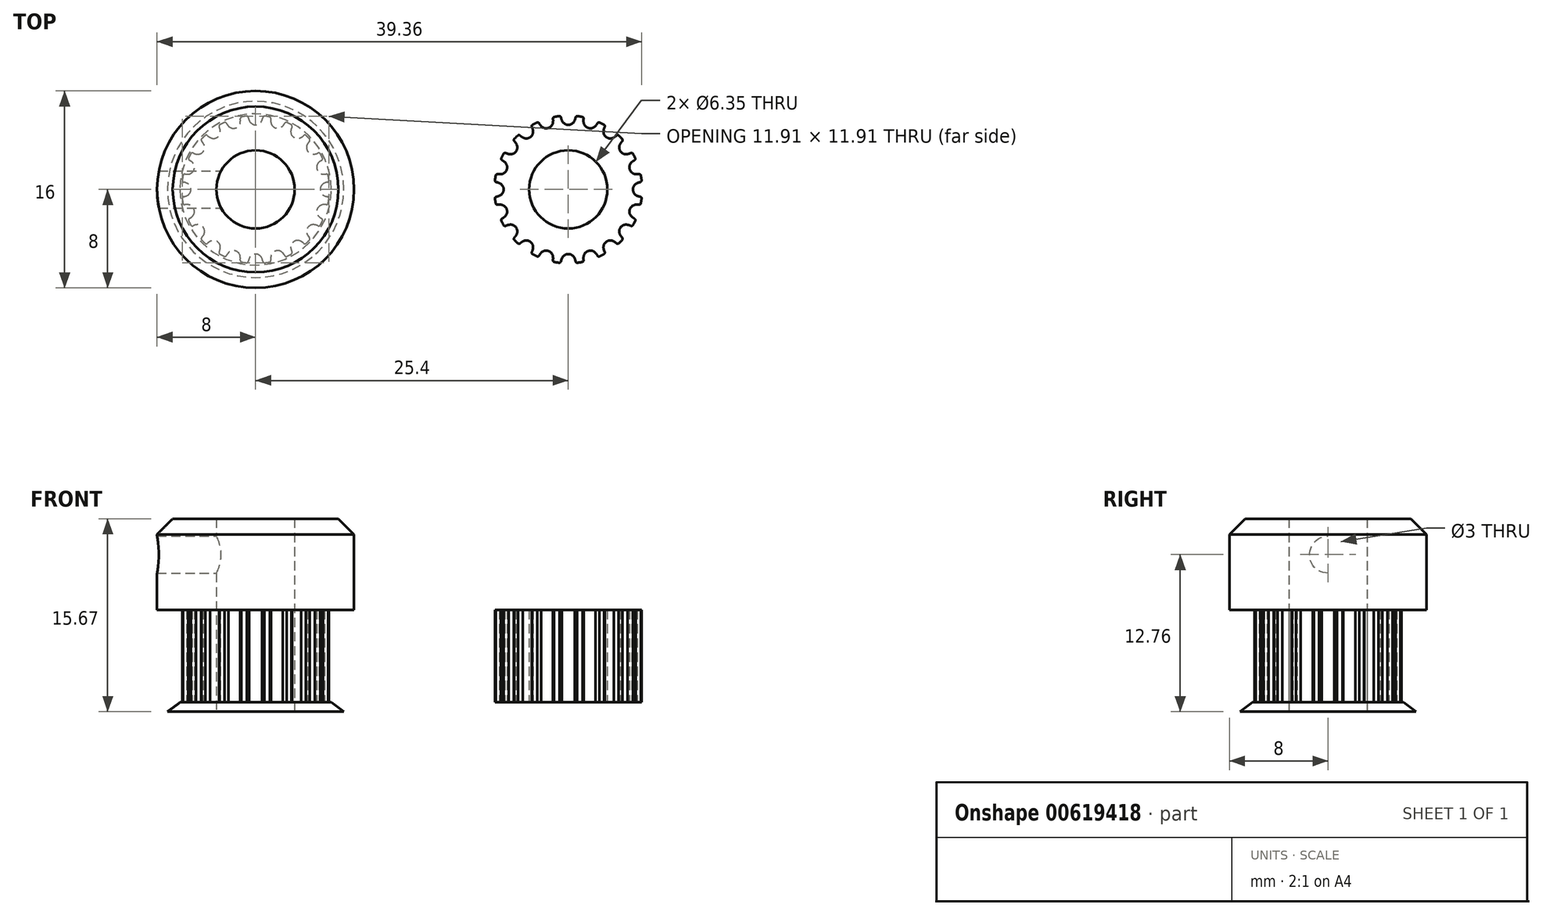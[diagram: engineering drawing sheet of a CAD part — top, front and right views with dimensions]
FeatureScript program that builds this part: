
annotation { "Feature Type Name" : "Feature", "Feature Type Description" : "" }
export const myFeature = defineFeature(function(context is Context, id is Id, definition is map)
    precondition{}
    {
        {
            var Q0;
            Q0=qCreatedBy(makeId("Top.planeOp"),FACE);
            var sketch = newSketch(context, id + "F0", { "sketchPlane" : qUnion([Q0])});
            skLineSegment(sketch, "E0", {"start": v(-19.17, 17.78) * mm, "end": v(-18.17, 17.78) * mm});
            skLineSegment(sketch, "E1", {"start": v(-18.17, 17.78) * mm, "end": v(-18.17, 18.4) * mm});
            skArc(sketch, "E2", {"start": v(-18.67, 18.85) * mm, "mid": v(-18.88, 19.07) * mm, "end": v(-19.17, 19.16) * mm});
            skArc(sketch, "E3", {"start": v(-18.58, 18.54) * mm, "mid": v(-18.61, 18.7) * mm, "end": v(-18.67, 18.85) * mm});
            skArc(sketch, "E4", {"start": v(-18.58, 18.54) * mm, "mid": v(-18.53, 18.44) * mm, "end": v(-18.43, 18.4) * mm});
            skLineSegment(sketch, "E5", {"start": v(-18.43, 18.4) * mm, "end": v(-18.17, 18.4) * mm});
            skArc(sketch, "E6.0.MirrorCS", {"start": v(-19.67, 18.85) * mm, "mid": v(-19.47, 19.07) * mm, "end": v(-19.17, 19.16) * mm});
            skArc(sketch, "E7.0.MirrorCS", {"start": v(-19.76, 18.54) * mm, "mid": v(-19.73, 18.7) * mm, "end": v(-19.67, 18.85) * mm});
            skArc(sketch, "E8.0.MirrorCS", {"start": v(-19.76, 18.54) * mm, "mid": v(-19.81, 18.44) * mm, "end": v(-19.91, 18.4) * mm});
            skLineSegment(sketch, "E9.0.MirrorCS", {"start": v(-19.91, 18.4) * mm, "end": v(-20.17, 18.4) * mm});
            skLineSegment(sketch, "E10.0.MirrorCS", {"start": v(-20.17, 17.78) * mm, "end": v(-20.17, 18.4) * mm});
            skLineSegment(sketch, "E11.0.MirrorCS", {"start": v(-19.17, 17.78) * mm, "end": v(-20.17, 17.78) * mm});
            skLineSegment(sketch, "E12.direction1", {"start": v(-20.17, 17.78) * mm, "end": v(-18.17, 17.78) * mm, "construction": true});
            skLineSegment(sketch, "E13", {"start": v(-20.17, 18.15) * mm, "end": v(-18.17, 18.15) * mm, "construction": true});
            skPoint(sketch, "E14", {"position": v(0, -5.25) * mm});
            skArc(sketch, "E15", {"start": v(0.51, -5.6) * mm, "mid": v(0, -5.25) * mm, "end": v(-0.51, -5.6) * mm});
            skArc(sketch, "E16", {"start": v(-0.51, -5.6) * mm, "mid": v(-0.56, -5.71) * mm, "end": v(-0.59, -5.83) * mm});
            skArc(sketch, "E17", {"start": v(0.59, -5.83) * mm, "mid": v(0.56, -5.71) * mm, "end": v(0.51, -5.6) * mm});
            skArc(sketch, "E18", {"start": v(0.72, -5.96) * mm, "mid": v(0.94, -5.93) * mm, "end": v(1.16, -5.89) * mm});
            skArc(sketch, "E19", {"start": v(0.59, -5.83) * mm, "mid": v(0.66, -5.94) * mm, "end": v(0.8, -5.95) * mm});
            skArc(sketch, "E20", {"start": v(-0.59, -5.83) * mm, "mid": v(-0.66, -5.94) * mm, "end": v(-0.8, -5.95) * mm});
            skArc(sketch, "E21.1.0", {"start": v(2.22, -5.16) * mm, "mid": v(1.62, -5) * mm, "end": v(1.24, -5.48) * mm});
            skPoint(sketch, "E21.1.1", {"position": v(1.62, -5) * mm});
            skArc(sketch, "E21.1.2", {"start": v(1.24, -5.48) * mm, "mid": v(1.23, -5.6) * mm, "end": v(1.24, -5.73) * mm});
            skArc(sketch, "E21.1.3", {"start": v(2.36, -5.37) * mm, "mid": v(2.47, -5.44) * mm, "end": v(2.6, -5.41) * mm});
            skArc(sketch, "E21.1.4", {"start": v(1.24, -5.73) * mm, "mid": v(1.2, -5.85) * mm, "end": v(1.08, -5.9) * mm});
            skArc(sketch, "E21.1.5", {"start": v(2.36, -5.37) * mm, "mid": v(2.3, -5.26) * mm, "end": v(2.22, -5.16) * mm});
            skArc(sketch, "E22.3.2.0", {"start": v(3.7, -4.22) * mm, "mid": v(3.09, -4.25) * mm, "end": v(2.87, -4.83) * mm});
            skPoint(sketch, "E22.4.2.0", {"position": v(3.09, -4.25) * mm});
            skArc(sketch, "E22.5.2.0", {"start": v(2.87, -4.83) * mm, "mid": v(2.9, -4.95) * mm, "end": v(2.95, -5.07) * mm});
            skArc(sketch, "E22.9.2.0", {"start": v(3.9, -4.37) * mm, "mid": v(4.03, -4.41) * mm, "end": v(4.14, -4.35) * mm});
            skArc(sketch, "E22.13.2.0", {"start": v(2.95, -5.07) * mm, "mid": v(2.95, -5.2) * mm, "end": v(2.85, -5.28) * mm});
            skArc(sketch, "E22.17.2.0", {"start": v(3.9, -4.37) * mm, "mid": v(3.81, -4.3) * mm, "end": v(3.7, -4.22) * mm});
            skArc(sketch, "E22.3.3.0", {"start": v(4.83, -2.87) * mm, "mid": v(4.25, -3.09) * mm, "end": v(4.22, -3.7) * mm});
            skPoint(sketch, "E22.4.3.0", {"position": v(4.25, -3.09) * mm});
            skArc(sketch, "E22.5.3.0", {"start": v(4.22, -3.7) * mm, "mid": v(4.3, -3.81) * mm, "end": v(4.37, -3.9) * mm});
            skArc(sketch, "E22.9.3.0", {"start": v(5.07, -2.95) * mm, "mid": v(5.2, -2.95) * mm, "end": v(5.28, -2.85) * mm});
            skArc(sketch, "E22.13.3.0", {"start": v(4.37, -3.9) * mm, "mid": v(4.41, -4.03) * mm, "end": v(4.35, -4.14) * mm});
            skArc(sketch, "E22.17.3.0", {"start": v(5.07, -2.95) * mm, "mid": v(4.95, -2.9) * mm, "end": v(4.83, -2.87) * mm});
            skArc(sketch, "E22.3.4.0", {"start": v(5.48, -1.24) * mm, "mid": v(5, -1.62) * mm, "end": v(5.16, -2.22) * mm});
            skPoint(sketch, "E22.4.4.0", {"position": v(5, -1.62) * mm});
            skArc(sketch, "E22.5.4.0", {"start": v(5.16, -2.22) * mm, "mid": v(5.26, -2.3) * mm, "end": v(5.37, -2.36) * mm});
            skArc(sketch, "E22.9.4.0", {"start": v(5.73, -1.24) * mm, "mid": v(5.85, -1.2) * mm, "end": v(5.9, -1.08) * mm});
            skArc(sketch, "E22.13.4.0", {"start": v(5.37, -2.36) * mm, "mid": v(5.44, -2.47) * mm, "end": v(5.41, -2.6) * mm});
            skArc(sketch, "E22.17.4.0", {"start": v(5.73, -1.24) * mm, "mid": v(5.6, -1.23) * mm, "end": v(5.48, -1.24) * mm});
            skArc(sketch, "E22.3.5.0", {"start": v(5.6, 0.51) * mm, "mid": v(5.25, 0) * mm, "end": v(5.6, -0.51) * mm});
            skPoint(sketch, "E22.4.5.0", {"position": v(5.25, 0) * mm});
            skArc(sketch, "E22.5.5.0", {"start": v(5.6, -0.51) * mm, "mid": v(5.71, -0.56) * mm, "end": v(5.83, -0.59) * mm});
            skArc(sketch, "E22.9.5.0", {"start": v(5.83, 0.59) * mm, "mid": v(5.94, 0.66) * mm, "end": v(5.95, 0.8) * mm});
            skArc(sketch, "E22.13.5.0", {"start": v(5.83, -0.59) * mm, "mid": v(5.94, -0.66) * mm, "end": v(5.95, -0.8) * mm});
            skArc(sketch, "E22.17.5.0", {"start": v(5.83, 0.59) * mm, "mid": v(5.71, 0.56) * mm, "end": v(5.6, 0.51) * mm});
            skArc(sketch, "E22.3.6.0", {"start": v(5.16, 2.22) * mm, "mid": v(5, 1.62) * mm, "end": v(5.48, 1.24) * mm});
            skPoint(sketch, "E22.4.6.0", {"position": v(5, 1.62) * mm});
            skArc(sketch, "E22.5.6.0", {"start": v(5.48, 1.24) * mm, "mid": v(5.6, 1.23) * mm, "end": v(5.73, 1.24) * mm});
            skArc(sketch, "E22.9.6.0", {"start": v(5.37, 2.36) * mm, "mid": v(5.44, 2.47) * mm, "end": v(5.41, 2.6) * mm});
            skArc(sketch, "E22.13.6.0", {"start": v(5.73, 1.24) * mm, "mid": v(5.85, 1.2) * mm, "end": v(5.9, 1.08) * mm});
            skArc(sketch, "E22.17.6.0", {"start": v(5.37, 2.36) * mm, "mid": v(5.26, 2.3) * mm, "end": v(5.16, 2.22) * mm});
            skArc(sketch, "E22.3.7.0", {"start": v(4.22, 3.7) * mm, "mid": v(4.25, 3.09) * mm, "end": v(4.83, 2.87) * mm});
            skPoint(sketch, "E22.4.7.0", {"position": v(4.25, 3.09) * mm});
            skArc(sketch, "E22.5.7.0", {"start": v(4.83, 2.87) * mm, "mid": v(4.95, 2.9) * mm, "end": v(5.07, 2.95) * mm});
            skArc(sketch, "E22.9.7.0", {"start": v(4.37, 3.9) * mm, "mid": v(4.41, 4.03) * mm, "end": v(4.35, 4.14) * mm});
            skArc(sketch, "E22.13.7.0", {"start": v(5.07, 2.95) * mm, "mid": v(5.2, 2.95) * mm, "end": v(5.28, 2.85) * mm});
            skArc(sketch, "E22.17.7.0", {"start": v(4.37, 3.9) * mm, "mid": v(4.3, 3.81) * mm, "end": v(4.22, 3.7) * mm});
            skArc(sketch, "E22.3.8.0", {"start": v(2.87, 4.83) * mm, "mid": v(3.09, 4.25) * mm, "end": v(3.7, 4.22) * mm});
            skPoint(sketch, "E22.4.8.0", {"position": v(3.09, 4.25) * mm});
            skArc(sketch, "E22.5.8.0", {"start": v(3.7, 4.22) * mm, "mid": v(3.81, 4.3) * mm, "end": v(3.9, 4.37) * mm});
            skArc(sketch, "E22.9.8.0", {"start": v(2.95, 5.07) * mm, "mid": v(2.95, 5.2) * mm, "end": v(2.85, 5.28) * mm});
            skArc(sketch, "E22.13.8.0", {"start": v(3.9, 4.37) * mm, "mid": v(4.03, 4.41) * mm, "end": v(4.14, 4.35) * mm});
            skArc(sketch, "E22.17.8.0", {"start": v(2.95, 5.07) * mm, "mid": v(2.9, 4.95) * mm, "end": v(2.87, 4.83) * mm});
            skArc(sketch, "E22.3.9.0", {"start": v(1.24, 5.48) * mm, "mid": v(1.62, 5) * mm, "end": v(2.22, 5.16) * mm});
            skPoint(sketch, "E22.4.9.0", {"position": v(1.62, 5) * mm});
            skArc(sketch, "E22.5.9.0", {"start": v(2.22, 5.16) * mm, "mid": v(2.3, 5.26) * mm, "end": v(2.36, 5.37) * mm});
            skArc(sketch, "E22.9.9.0", {"start": v(1.24, 5.73) * mm, "mid": v(1.2, 5.85) * mm, "end": v(1.08, 5.9) * mm});
            skArc(sketch, "E22.13.9.0", {"start": v(2.36, 5.37) * mm, "mid": v(2.47, 5.44) * mm, "end": v(2.6, 5.41) * mm});
            skArc(sketch, "E22.17.9.0", {"start": v(1.24, 5.73) * mm, "mid": v(1.23, 5.6) * mm, "end": v(1.24, 5.48) * mm});
            skArc(sketch, "E22.3.10.0", {"start": v(-0.51, 5.6) * mm, "mid": v(0, 5.25) * mm, "end": v(0.51, 5.6) * mm});
            skPoint(sketch, "E22.4.10.0", {"position": v(0, 5.25) * mm});
            skArc(sketch, "E22.5.10.0", {"start": v(0.51, 5.6) * mm, "mid": v(0.56, 5.71) * mm, "end": v(0.59, 5.83) * mm});
            skArc(sketch, "E22.9.10.0", {"start": v(-0.59, 5.83) * mm, "mid": v(-0.66, 5.94) * mm, "end": v(-0.8, 5.95) * mm});
            skArc(sketch, "E22.13.10.0", {"start": v(0.59, 5.83) * mm, "mid": v(0.66, 5.94) * mm, "end": v(0.8, 5.95) * mm});
            skArc(sketch, "E22.17.10.0", {"start": v(-0.59, 5.83) * mm, "mid": v(-0.56, 5.71) * mm, "end": v(-0.51, 5.6) * mm});
            skArc(sketch, "E22.3.11.0", {"start": v(-2.22, 5.16) * mm, "mid": v(-1.62, 5) * mm, "end": v(-1.24, 5.48) * mm});
            skPoint(sketch, "E22.4.11.0", {"position": v(-1.62, 5) * mm});
            skArc(sketch, "E22.5.11.0", {"start": v(-1.24, 5.48) * mm, "mid": v(-1.23, 5.6) * mm, "end": v(-1.24, 5.73) * mm});
            skArc(sketch, "E22.9.11.0", {"start": v(-2.36, 5.37) * mm, "mid": v(-2.47, 5.44) * mm, "end": v(-2.6, 5.41) * mm});
            skArc(sketch, "E22.13.11.0", {"start": v(-1.24, 5.73) * mm, "mid": v(-1.2, 5.85) * mm, "end": v(-1.08, 5.9) * mm});
            skArc(sketch, "E22.17.11.0", {"start": v(-2.36, 5.37) * mm, "mid": v(-2.3, 5.26) * mm, "end": v(-2.22, 5.16) * mm});
            skArc(sketch, "E22.3.12.0", {"start": v(-3.7, 4.22) * mm, "mid": v(-3.09, 4.25) * mm, "end": v(-2.87, 4.83) * mm});
            skPoint(sketch, "E22.4.12.0", {"position": v(-3.09, 4.25) * mm});
            skArc(sketch, "E22.5.12.0", {"start": v(-2.87, 4.83) * mm, "mid": v(-2.9, 4.95) * mm, "end": v(-2.95, 5.07) * mm});
            skArc(sketch, "E22.9.12.0", {"start": v(-3.9, 4.37) * mm, "mid": v(-4.03, 4.41) * mm, "end": v(-4.14, 4.35) * mm});
            skArc(sketch, "E22.13.12.0", {"start": v(-2.95, 5.07) * mm, "mid": v(-2.95, 5.2) * mm, "end": v(-2.85, 5.28) * mm});
            skArc(sketch, "E22.17.12.0", {"start": v(-3.9, 4.37) * mm, "mid": v(-3.81, 4.3) * mm, "end": v(-3.7, 4.22) * mm});
            skArc(sketch, "E22.3.13.0", {"start": v(-4.83, 2.87) * mm, "mid": v(-4.25, 3.09) * mm, "end": v(-4.22, 3.7) * mm});
            skPoint(sketch, "E22.4.13.0", {"position": v(-4.25, 3.09) * mm});
            skArc(sketch, "E22.5.13.0", {"start": v(-4.22, 3.7) * mm, "mid": v(-4.3, 3.81) * mm, "end": v(-4.37, 3.9) * mm});
            skArc(sketch, "E22.9.13.0", {"start": v(-5.07, 2.95) * mm, "mid": v(-5.2, 2.95) * mm, "end": v(-5.28, 2.85) * mm});
            skArc(sketch, "E22.13.13.0", {"start": v(-4.37, 3.9) * mm, "mid": v(-4.41, 4.03) * mm, "end": v(-4.35, 4.14) * mm});
            skArc(sketch, "E22.17.13.0", {"start": v(-5.07, 2.95) * mm, "mid": v(-4.95, 2.9) * mm, "end": v(-4.83, 2.87) * mm});
            skArc(sketch, "E22.3.14.0", {"start": v(-5.48, 1.24) * mm, "mid": v(-5, 1.62) * mm, "end": v(-5.16, 2.22) * mm});
            skPoint(sketch, "E22.4.14.0", {"position": v(-5, 1.62) * mm});
            skArc(sketch, "E22.5.14.0", {"start": v(-5.16, 2.22) * mm, "mid": v(-5.26, 2.3) * mm, "end": v(-5.37, 2.36) * mm});
            skArc(sketch, "E22.9.14.0", {"start": v(-5.73, 1.24) * mm, "mid": v(-5.85, 1.2) * mm, "end": v(-5.9, 1.08) * mm});
            skArc(sketch, "E22.13.14.0", {"start": v(-5.37, 2.36) * mm, "mid": v(-5.44, 2.47) * mm, "end": v(-5.41, 2.6) * mm});
            skArc(sketch, "E22.17.14.0", {"start": v(-5.73, 1.24) * mm, "mid": v(-5.6, 1.23) * mm, "end": v(-5.48, 1.24) * mm});
            skArc(sketch, "E22.3.15.0", {"start": v(-5.6, -0.51) * mm, "mid": v(-5.25, 0) * mm, "end": v(-5.6, 0.51) * mm});
            skPoint(sketch, "E22.4.15.0", {"position": v(-5.25, 0) * mm});
            skArc(sketch, "E22.5.15.0", {"start": v(-5.6, 0.51) * mm, "mid": v(-5.71, 0.56) * mm, "end": v(-5.83, 0.59) * mm});
            skArc(sketch, "E22.9.15.0", {"start": v(-5.83, -0.59) * mm, "mid": v(-5.94, -0.66) * mm, "end": v(-5.95, -0.8) * mm});
            skArc(sketch, "E22.13.15.0", {"start": v(-5.83, 0.59) * mm, "mid": v(-5.94, 0.66) * mm, "end": v(-5.95, 0.8) * mm});
            skArc(sketch, "E22.17.15.0", {"start": v(-5.83, -0.59) * mm, "mid": v(-5.71, -0.56) * mm, "end": v(-5.6, -0.51) * mm});
            skArc(sketch, "E22.3.16.0", {"start": v(-5.16, -2.22) * mm, "mid": v(-5, -1.62) * mm, "end": v(-5.48, -1.24) * mm});
            skPoint(sketch, "E22.4.16.0", {"position": v(-5, -1.62) * mm});
            skArc(sketch, "E22.5.16.0", {"start": v(-5.48, -1.24) * mm, "mid": v(-5.6, -1.23) * mm, "end": v(-5.73, -1.24) * mm});
            skArc(sketch, "E22.9.16.0", {"start": v(-5.37, -2.36) * mm, "mid": v(-5.44, -2.47) * mm, "end": v(-5.41, -2.6) * mm});
            skArc(sketch, "E22.13.16.0", {"start": v(-5.73, -1.24) * mm, "mid": v(-5.85, -1.2) * mm, "end": v(-5.9, -1.08) * mm});
            skArc(sketch, "E22.17.16.0", {"start": v(-5.37, -2.36) * mm, "mid": v(-5.26, -2.3) * mm, "end": v(-5.16, -2.22) * mm});
            skArc(sketch, "E22.3.17.0", {"start": v(-4.22, -3.7) * mm, "mid": v(-4.25, -3.09) * mm, "end": v(-4.83, -2.87) * mm});
            skPoint(sketch, "E22.4.17.0", {"position": v(-4.25, -3.09) * mm});
            skArc(sketch, "E22.5.17.0", {"start": v(-4.83, -2.87) * mm, "mid": v(-4.95, -2.9) * mm, "end": v(-5.07, -2.95) * mm});
            skArc(sketch, "E22.9.17.0", {"start": v(-4.37, -3.9) * mm, "mid": v(-4.41, -4.03) * mm, "end": v(-4.35, -4.14) * mm});
            skArc(sketch, "E22.13.17.0", {"start": v(-5.07, -2.95) * mm, "mid": v(-5.2, -2.95) * mm, "end": v(-5.28, -2.85) * mm});
            skArc(sketch, "E22.17.17.0", {"start": v(-4.37, -3.9) * mm, "mid": v(-4.3, -3.81) * mm, "end": v(-4.22, -3.7) * mm});
            skArc(sketch, "E22.3.18.0", {"start": v(-2.87, -4.83) * mm, "mid": v(-3.09, -4.25) * mm, "end": v(-3.7, -4.22) * mm});
            skPoint(sketch, "E22.4.18.0", {"position": v(-3.09, -4.25) * mm});
            skArc(sketch, "E22.5.18.0", {"start": v(-3.7, -4.22) * mm, "mid": v(-3.81, -4.3) * mm, "end": v(-3.9, -4.37) * mm});
            skArc(sketch, "E22.9.18.0", {"start": v(-2.95, -5.07) * mm, "mid": v(-2.95, -5.2) * mm, "end": v(-2.85, -5.28) * mm});
            skArc(sketch, "E22.13.18.0", {"start": v(-3.9, -4.37) * mm, "mid": v(-4.03, -4.41) * mm, "end": v(-4.14, -4.35) * mm});
            skArc(sketch, "E22.17.18.0", {"start": v(-2.95, -5.07) * mm, "mid": v(-2.9, -4.95) * mm, "end": v(-2.87, -4.83) * mm});
            skArc(sketch, "E22.3.19.0", {"start": v(-1.24, -5.48) * mm, "mid": v(-1.62, -5) * mm, "end": v(-2.22, -5.16) * mm});
            skPoint(sketch, "E22.4.19.0", {"position": v(-1.62, -5) * mm});
            skArc(sketch, "E22.5.19.0", {"start": v(-2.22, -5.16) * mm, "mid": v(-2.3, -5.26) * mm, "end": v(-2.36, -5.37) * mm});
            skArc(sketch, "E22.9.19.0", {"start": v(-1.24, -5.73) * mm, "mid": v(-1.2, -5.85) * mm, "end": v(-1.08, -5.9) * mm});
            skArc(sketch, "E22.13.19.0", {"start": v(-2.36, -5.37) * mm, "mid": v(-2.47, -5.44) * mm, "end": v(-2.6, -5.41) * mm});
            skArc(sketch, "E22.17.19.0", {"start": v(-1.24, -5.73) * mm, "mid": v(-1.23, -5.6) * mm, "end": v(-1.24, -5.48) * mm});
            skArc(sketch, "E23.trimOffspring", {"start": v(2.52, -5.44) * mm, "mid": v(2.72, -5.35) * mm, "end": v(2.92, -5.24) * mm});
            skArc(sketch, "E24.trimOffspring", {"start": v(4.08, -4.4) * mm, "mid": v(4.24, -4.24) * mm, "end": v(4.4, -4.08) * mm});
            skArc(sketch, "E25.trimOffspring", {"start": v(5.24, -2.92) * mm, "mid": v(5.33, -2.76) * mm, "end": v(5.41, -2.6) * mm});
            skArc(sketch, "E26.trimOffspring", {"start": v(5.89, -1.16) * mm, "mid": v(5.93, -0.94) * mm, "end": v(5.96, -0.72) * mm});
            skArc(sketch, "E27.trimOffspring", {"start": v(5.44, 2.52) * mm, "mid": v(5.35, 2.72) * mm, "end": v(5.24, 2.92) * mm});
            skArc(sketch, "E28.trimOffspring", {"start": v(4.4, 4.08) * mm, "mid": v(4.24, 4.24) * mm, "end": v(4.08, 4.4) * mm});
            skArc(sketch, "E29.trimOffspring", {"start": v(5.96, 0.72) * mm, "mid": v(5.93, 0.94) * mm, "end": v(5.89, 1.16) * mm});
            skArc(sketch, "E30.trimOffspring", {"start": v(2.92, 5.24) * mm, "mid": v(2.72, 5.35) * mm, "end": v(2.52, 5.44) * mm});
            skArc(sketch, "E31.trimOffspring", {"start": v(1.16, 5.89) * mm, "mid": v(0.94, 5.93) * mm, "end": v(0.72, 5.96) * mm});
            skArc(sketch, "E32.trimOffspring", {"start": v(-0.72, 5.96) * mm, "mid": v(-0.94, 5.93) * mm, "end": v(-1.16, 5.89) * mm});
            skArc(sketch, "E33.trimOffspring", {"start": v(-2.52, 5.44) * mm, "mid": v(-2.72, 5.35) * mm, "end": v(-2.92, 5.24) * mm});
            skArc(sketch, "E34.trimOffspring", {"start": v(-4.08, 4.4) * mm, "mid": v(-4.24, 4.24) * mm, "end": v(-4.4, 4.08) * mm});
            skArc(sketch, "E35.trimOffspring", {"start": v(-5.24, 2.92) * mm, "mid": v(-5.35, 2.72) * mm, "end": v(-5.44, 2.52) * mm});
            skArc(sketch, "E36.trimOffspring", {"start": v(-5.89, 1.16) * mm, "mid": v(-5.93, 0.94) * mm, "end": v(-5.96, 0.72) * mm});
            skArc(sketch, "E37.trimOffspring", {"start": v(-5.96, -0.72) * mm, "mid": v(-5.93, -0.94) * mm, "end": v(-5.89, -1.16) * mm});
            skArc(sketch, "E38.trimOffspring", {"start": v(-5.44, -2.52) * mm, "mid": v(-5.35, -2.72) * mm, "end": v(-5.24, -2.92) * mm});
            skArc(sketch, "E39.trimOffspring", {"start": v(-4.4, -4.08) * mm, "mid": v(-4.24, -4.24) * mm, "end": v(-4.08, -4.4) * mm});
            skArc(sketch, "E40.trimOffspring", {"start": v(-2.92, -5.24) * mm, "mid": v(-2.72, -5.35) * mm, "end": v(-2.52, -5.44) * mm});
            skArc(sketch, "E41.trimOffspring", {"start": v(-1.16, -5.89) * mm, "mid": v(-0.94, -5.93) * mm, "end": v(-0.72, -5.96) * mm});
            skSolve(sketch);
        }
        {
            var Q0;
            Q0=makeQuery(id+"F0.imprint","IMPRINT",FACE,{"disambiguationData":[TD([[makeQuery(id+"F0.imprint","IMPRINT",EDGE,{"derivedFrom":sQuery(id+"F0.wireOp",EDGE,"E15")}),-1.0]])]});
            extrude(context, id + "F1", {"entities" : qUnion([Q0]), "depth" : 7.5 * mm});
        }
        {
            var Q0;
            Q0=makeQuery(id+"F1.opExtrude","CAP_FACE",FACE,{"disambiguationData":[OSD([sQuery(id+"F0.wireOp",EDGE,"E15"),sQuery(id+"F0.wireOp",EDGE,"E16"),sQuery(id+"F0.wireOp",EDGE,"E17"),sQuery(id+"F0.wireOp",EDGE,"E18"),sQuery(id+"F0.wireOp",EDGE,"E19"),sQuery(id+"F0.wireOp",EDGE,"E20"),sQuery(id+"F0.wireOp",EDGE,"E21.1.0"),sQuery(id+"F0.wireOp",EDGE,"E21.1.2"),sQuery(id+"F0.wireOp",EDGE,"E21.1.3"),sQuery(id+"F0.wireOp",EDGE,"E21.1.4"),sQuery(id+"F0.wireOp",EDGE,"E21.1.5"),sQuery(id+"F0.wireOp",EDGE,"E22.3.2.0"),sQuery(id+"F0.wireOp",EDGE,"E22.5.2.0"),sQuery(id+"F0.wireOp",EDGE,"E22.9.2.0"),sQuery(id+"F0.wireOp",EDGE,"E22.13.2.0"),sQuery(id+"F0.wireOp",EDGE,"E22.17.2.0"),sQuery(id+"F0.wireOp",EDGE,"E22.3.3.0"),sQuery(id+"F0.wireOp",EDGE,"E22.5.3.0"),sQuery(id+"F0.wireOp",EDGE,"E22.9.3.0"),sQuery(id+"F0.wireOp",EDGE,"E22.13.3.0"),sQuery(id+"F0.wireOp",EDGE,"E22.17.3.0"),sQuery(id+"F0.wireOp",EDGE,"E22.3.4.0"),sQuery(id+"F0.wireOp",EDGE,"E22.5.4.0"),sQuery(id+"F0.wireOp",EDGE,"E22.9.4.0"),sQuery(id+"F0.wireOp",EDGE,"E22.13.4.0"),sQuery(id+"F0.wireOp",EDGE,"E22.17.4.0"),sQuery(id+"F0.wireOp",EDGE,"E22.3.5.0"),sQuery(id+"F0.wireOp",EDGE,"E22.5.5.0"),sQuery(id+"F0.wireOp",EDGE,"E22.9.5.0"),sQuery(id+"F0.wireOp",EDGE,"E22.13.5.0"),sQuery(id+"F0.wireOp",EDGE,"E22.17.5.0"),sQuery(id+"F0.wireOp",EDGE,"E22.3.6.0"),sQuery(id+"F0.wireOp",EDGE,"E22.5.6.0"),sQuery(id+"F0.wireOp",EDGE,"E22.9.6.0"),sQuery(id+"F0.wireOp",EDGE,"E22.13.6.0"),sQuery(id+"F0.wireOp",EDGE,"E22.17.6.0"),sQuery(id+"F0.wireOp",EDGE,"E22.3.7.0"),sQuery(id+"F0.wireOp",EDGE,"E22.5.7.0"),sQuery(id+"F0.wireOp",EDGE,"E22.9.7.0"),sQuery(id+"F0.wireOp",EDGE,"E22.13.7.0"),sQuery(id+"F0.wireOp",EDGE,"E22.17.7.0"),sQuery(id+"F0.wireOp",EDGE,"E22.3.8.0"),sQuery(id+"F0.wireOp",EDGE,"E22.5.8.0"),sQuery(id+"F0.wireOp",EDGE,"E22.9.8.0"),sQuery(id+"F0.wireOp",EDGE,"E22.13.8.0"),sQuery(id+"F0.wireOp",EDGE,"E22.17.8.0"),sQuery(id+"F0.wireOp",EDGE,"E22.3.9.0"),sQuery(id+"F0.wireOp",EDGE,"E22.5.9.0"),sQuery(id+"F0.wireOp",EDGE,"E22.9.9.0"),sQuery(id+"F0.wireOp",EDGE,"E22.13.9.0"),sQuery(id+"F0.wireOp",EDGE,"E22.17.9.0"),sQuery(id+"F0.wireOp",EDGE,"E22.3.10.0"),sQuery(id+"F0.wireOp",EDGE,"E22.5.10.0"),sQuery(id+"F0.wireOp",EDGE,"E22.9.10.0"),sQuery(id+"F0.wireOp",EDGE,"E22.13.10.0"),sQuery(id+"F0.wireOp",EDGE,"E22.17.10.0"),sQuery(id+"F0.wireOp",EDGE,"E22.3.11.0"),sQuery(id+"F0.wireOp",EDGE,"E22.5.11.0"),sQuery(id+"F0.wireOp",EDGE,"E22.9.11.0"),sQuery(id+"F0.wireOp",EDGE,"E22.13.11.0"),sQuery(id+"F0.wireOp",EDGE,"E22.17.11.0"),sQuery(id+"F0.wireOp",EDGE,"E22.3.12.0"),sQuery(id+"F0.wireOp",EDGE,"E22.5.12.0"),sQuery(id+"F0.wireOp",EDGE,"E22.9.12.0"),sQuery(id+"F0.wireOp",EDGE,"E22.13.12.0"),sQuery(id+"F0.wireOp",EDGE,"E22.17.12.0"),sQuery(id+"F0.wireOp",EDGE,"E22.3.13.0"),sQuery(id+"F0.wireOp",EDGE,"E22.5.13.0"),sQuery(id+"F0.wireOp",EDGE,"E22.9.13.0"),sQuery(id+"F0.wireOp",EDGE,"E22.13.13.0"),sQuery(id+"F0.wireOp",EDGE,"E22.17.13.0"),sQuery(id+"F0.wireOp",EDGE,"E22.3.14.0"),sQuery(id+"F0.wireOp",EDGE,"E22.5.14.0"),sQuery(id+"F0.wireOp",EDGE,"E22.9.14.0"),sQuery(id+"F0.wireOp",EDGE,"E22.13.14.0"),sQuery(id+"F0.wireOp",EDGE,"E22.17.14.0"),sQuery(id+"F0.wireOp",EDGE,"E22.3.15.0"),sQuery(id+"F0.wireOp",EDGE,"E22.5.15.0"),sQuery(id+"F0.wireOp",EDGE,"E22.9.15.0"),sQuery(id+"F0.wireOp",EDGE,"E22.13.15.0"),sQuery(id+"F0.wireOp",EDGE,"E22.17.15.0"),sQuery(id+"F0.wireOp",EDGE,"E22.3.16.0"),sQuery(id+"F0.wireOp",EDGE,"E22.5.16.0"),sQuery(id+"F0.wireOp",EDGE,"E22.9.16.0"),sQuery(id+"F0.wireOp",EDGE,"E22.13.16.0"),sQuery(id+"F0.wireOp",EDGE,"E22.17.16.0"),sQuery(id+"F0.wireOp",EDGE,"E22.3.17.0"),sQuery(id+"F0.wireOp",EDGE,"E22.5.17.0"),sQuery(id+"F0.wireOp",EDGE,"E22.9.17.0"),sQuery(id+"F0.wireOp",EDGE,"E22.13.17.0"),sQuery(id+"F0.wireOp",EDGE,"E22.17.17.0"),sQuery(id+"F0.wireOp",EDGE,"E22.3.18.0"),sQuery(id+"F0.wireOp",EDGE,"E22.5.18.0"),sQuery(id+"F0.wireOp",EDGE,"E22.9.18.0"),sQuery(id+"F0.wireOp",EDGE,"E22.13.18.0"),sQuery(id+"F0.wireOp",EDGE,"E22.17.18.0"),sQuery(id+"F0.wireOp",EDGE,"E22.3.19.0"),sQuery(id+"F0.wireOp",EDGE,"E22.5.19.0"),sQuery(id+"F0.wireOp",EDGE,"E22.9.19.0"),sQuery(id+"F0.wireOp",EDGE,"E22.13.19.0"),sQuery(id+"F0.wireOp",EDGE,"E22.17.19.0"),sQuery(id+"F0.wireOp",EDGE,"E23.trimOffspring"),sQuery(id+"F0.wireOp",EDGE,"E24.trimOffspring"),sQuery(id+"F0.wireOp",EDGE,"E25.trimOffspring"),sQuery(id+"F0.wireOp",EDGE,"E26.trimOffspring"),sQuery(id+"F0.wireOp",EDGE,"E27.trimOffspring"),sQuery(id+"F0.wireOp",EDGE,"E28.trimOffspring"),sQuery(id+"F0.wireOp",EDGE,"E29.trimOffspring"),sQuery(id+"F0.wireOp",EDGE,"E30.trimOffspring"),sQuery(id+"F0.wireOp",EDGE,"E31.trimOffspring"),sQuery(id+"F0.wireOp",EDGE,"E32.trimOffspring"),sQuery(id+"F0.wireOp",EDGE,"E33.trimOffspring"),sQuery(id+"F0.wireOp",EDGE,"E34.trimOffspring"),sQuery(id+"F0.wireOp",EDGE,"E35.trimOffspring"),sQuery(id+"F0.wireOp",EDGE,"E36.trimOffspring"),sQuery(id+"F0.wireOp",EDGE,"E37.trimOffspring"),sQuery(id+"F0.wireOp",EDGE,"E38.trimOffspring"),sQuery(id+"F0.wireOp",EDGE,"E39.trimOffspring"),sQuery(id+"F0.wireOp",EDGE,"E40.trimOffspring"),sQuery(id+"F0.wireOp",EDGE,"E41.trimOffspring")])],"isStart":false});
            var sketch = newSketch(context, id + "F2", { "sketchPlane" : qUnion([Q0])});
            skCircle(sketch, "E42", {"center": v(0, 0) * mm, "radius": 8 * mm});
            skSolve(sketch);
        }
        {
            var Q0;
            Q0=qSketchRegion(id+"F2",true);
            extrude(context, id + "F3", {"entities" : qUnion([Q0]), "operationType" : NewBodyOperationType.ADD, "depth" : 9 * mm});
        }
        {
            var Q0;
            Q0=makeQuery(id+"F1.opExtrude","CAP_FACE",FACE,{"disambiguationData":[OSD([sQuery(id+"F0.wireOp",EDGE,"E15"),sQuery(id+"F0.wireOp",EDGE,"E16"),sQuery(id+"F0.wireOp",EDGE,"E17"),sQuery(id+"F0.wireOp",EDGE,"E18"),sQuery(id+"F0.wireOp",EDGE,"E19"),sQuery(id+"F0.wireOp",EDGE,"E20"),sQuery(id+"F0.wireOp",EDGE,"E21.1.0"),sQuery(id+"F0.wireOp",EDGE,"E21.1.2"),sQuery(id+"F0.wireOp",EDGE,"E21.1.3"),sQuery(id+"F0.wireOp",EDGE,"E21.1.4"),sQuery(id+"F0.wireOp",EDGE,"E21.1.5"),sQuery(id+"F0.wireOp",EDGE,"E22.3.2.0"),sQuery(id+"F0.wireOp",EDGE,"E22.5.2.0"),sQuery(id+"F0.wireOp",EDGE,"E22.9.2.0"),sQuery(id+"F0.wireOp",EDGE,"E22.13.2.0"),sQuery(id+"F0.wireOp",EDGE,"E22.17.2.0"),sQuery(id+"F0.wireOp",EDGE,"E22.3.3.0"),sQuery(id+"F0.wireOp",EDGE,"E22.5.3.0"),sQuery(id+"F0.wireOp",EDGE,"E22.9.3.0"),sQuery(id+"F0.wireOp",EDGE,"E22.13.3.0"),sQuery(id+"F0.wireOp",EDGE,"E22.17.3.0"),sQuery(id+"F0.wireOp",EDGE,"E22.3.4.0"),sQuery(id+"F0.wireOp",EDGE,"E22.5.4.0"),sQuery(id+"F0.wireOp",EDGE,"E22.9.4.0"),sQuery(id+"F0.wireOp",EDGE,"E22.13.4.0"),sQuery(id+"F0.wireOp",EDGE,"E22.17.4.0"),sQuery(id+"F0.wireOp",EDGE,"E22.3.5.0"),sQuery(id+"F0.wireOp",EDGE,"E22.5.5.0"),sQuery(id+"F0.wireOp",EDGE,"E22.9.5.0"),sQuery(id+"F0.wireOp",EDGE,"E22.13.5.0"),sQuery(id+"F0.wireOp",EDGE,"E22.17.5.0"),sQuery(id+"F0.wireOp",EDGE,"E22.3.6.0"),sQuery(id+"F0.wireOp",EDGE,"E22.5.6.0"),sQuery(id+"F0.wireOp",EDGE,"E22.9.6.0"),sQuery(id+"F0.wireOp",EDGE,"E22.13.6.0"),sQuery(id+"F0.wireOp",EDGE,"E22.17.6.0"),sQuery(id+"F0.wireOp",EDGE,"E22.3.7.0"),sQuery(id+"F0.wireOp",EDGE,"E22.5.7.0"),sQuery(id+"F0.wireOp",EDGE,"E22.9.7.0"),sQuery(id+"F0.wireOp",EDGE,"E22.13.7.0"),sQuery(id+"F0.wireOp",EDGE,"E22.17.7.0"),sQuery(id+"F0.wireOp",EDGE,"E22.3.8.0"),sQuery(id+"F0.wireOp",EDGE,"E22.5.8.0"),sQuery(id+"F0.wireOp",EDGE,"E22.9.8.0"),sQuery(id+"F0.wireOp",EDGE,"E22.13.8.0"),sQuery(id+"F0.wireOp",EDGE,"E22.17.8.0"),sQuery(id+"F0.wireOp",EDGE,"E22.3.9.0"),sQuery(id+"F0.wireOp",EDGE,"E22.5.9.0"),sQuery(id+"F0.wireOp",EDGE,"E22.9.9.0"),sQuery(id+"F0.wireOp",EDGE,"E22.13.9.0"),sQuery(id+"F0.wireOp",EDGE,"E22.17.9.0"),sQuery(id+"F0.wireOp",EDGE,"E22.3.10.0"),sQuery(id+"F0.wireOp",EDGE,"E22.5.10.0"),sQuery(id+"F0.wireOp",EDGE,"E22.9.10.0"),sQuery(id+"F0.wireOp",EDGE,"E22.13.10.0"),sQuery(id+"F0.wireOp",EDGE,"E22.17.10.0"),sQuery(id+"F0.wireOp",EDGE,"E22.3.11.0"),sQuery(id+"F0.wireOp",EDGE,"E22.5.11.0"),sQuery(id+"F0.wireOp",EDGE,"E22.9.11.0"),sQuery(id+"F0.wireOp",EDGE,"E22.13.11.0"),sQuery(id+"F0.wireOp",EDGE,"E22.17.11.0"),sQuery(id+"F0.wireOp",EDGE,"E22.3.12.0"),sQuery(id+"F0.wireOp",EDGE,"E22.5.12.0"),sQuery(id+"F0.wireOp",EDGE,"E22.9.12.0"),sQuery(id+"F0.wireOp",EDGE,"E22.13.12.0"),sQuery(id+"F0.wireOp",EDGE,"E22.17.12.0"),sQuery(id+"F0.wireOp",EDGE,"E22.3.13.0"),sQuery(id+"F0.wireOp",EDGE,"E22.5.13.0"),sQuery(id+"F0.wireOp",EDGE,"E22.9.13.0"),sQuery(id+"F0.wireOp",EDGE,"E22.13.13.0"),sQuery(id+"F0.wireOp",EDGE,"E22.17.13.0"),sQuery(id+"F0.wireOp",EDGE,"E22.3.14.0"),sQuery(id+"F0.wireOp",EDGE,"E22.5.14.0"),sQuery(id+"F0.wireOp",EDGE,"E22.9.14.0"),sQuery(id+"F0.wireOp",EDGE,"E22.13.14.0"),sQuery(id+"F0.wireOp",EDGE,"E22.17.14.0"),sQuery(id+"F0.wireOp",EDGE,"E22.3.15.0"),sQuery(id+"F0.wireOp",EDGE,"E22.5.15.0"),sQuery(id+"F0.wireOp",EDGE,"E22.9.15.0"),sQuery(id+"F0.wireOp",EDGE,"E22.13.15.0"),sQuery(id+"F0.wireOp",EDGE,"E22.17.15.0"),sQuery(id+"F0.wireOp",EDGE,"E22.3.16.0"),sQuery(id+"F0.wireOp",EDGE,"E22.5.16.0"),sQuery(id+"F0.wireOp",EDGE,"E22.9.16.0"),sQuery(id+"F0.wireOp",EDGE,"E22.13.16.0"),sQuery(id+"F0.wireOp",EDGE,"E22.17.16.0"),sQuery(id+"F0.wireOp",EDGE,"E22.3.17.0"),sQuery(id+"F0.wireOp",EDGE,"E22.5.17.0"),sQuery(id+"F0.wireOp",EDGE,"E22.9.17.0"),sQuery(id+"F0.wireOp",EDGE,"E22.13.17.0"),sQuery(id+"F0.wireOp",EDGE,"E22.17.17.0"),sQuery(id+"F0.wireOp",EDGE,"E22.3.18.0"),sQuery(id+"F0.wireOp",EDGE,"E22.5.18.0"),sQuery(id+"F0.wireOp",EDGE,"E22.9.18.0"),sQuery(id+"F0.wireOp",EDGE,"E22.13.18.0"),sQuery(id+"F0.wireOp",EDGE,"E22.17.18.0"),sQuery(id+"F0.wireOp",EDGE,"E22.3.19.0"),sQuery(id+"F0.wireOp",EDGE,"E22.5.19.0"),sQuery(id+"F0.wireOp",EDGE,"E22.9.19.0"),sQuery(id+"F0.wireOp",EDGE,"E22.13.19.0"),sQuery(id+"F0.wireOp",EDGE,"E22.17.19.0"),sQuery(id+"F0.wireOp",EDGE,"E23.trimOffspring"),sQuery(id+"F0.wireOp",EDGE,"E24.trimOffspring"),sQuery(id+"F0.wireOp",EDGE,"E25.trimOffspring"),sQuery(id+"F0.wireOp",EDGE,"E26.trimOffspring"),sQuery(id+"F0.wireOp",EDGE,"E27.trimOffspring"),sQuery(id+"F0.wireOp",EDGE,"E28.trimOffspring"),sQuery(id+"F0.wireOp",EDGE,"E29.trimOffspring"),sQuery(id+"F0.wireOp",EDGE,"E30.trimOffspring"),sQuery(id+"F0.wireOp",EDGE,"E31.trimOffspring"),sQuery(id+"F0.wireOp",EDGE,"E32.trimOffspring"),sQuery(id+"F0.wireOp",EDGE,"E33.trimOffspring"),sQuery(id+"F0.wireOp",EDGE,"E34.trimOffspring"),sQuery(id+"F0.wireOp",EDGE,"E35.trimOffspring"),sQuery(id+"F0.wireOp",EDGE,"E36.trimOffspring"),sQuery(id+"F0.wireOp",EDGE,"E37.trimOffspring"),sQuery(id+"F0.wireOp",EDGE,"E38.trimOffspring"),sQuery(id+"F0.wireOp",EDGE,"E39.trimOffspring"),sQuery(id+"F0.wireOp",EDGE,"E40.trimOffspring"),sQuery(id+"F0.wireOp",EDGE,"E41.trimOffspring")])],"isStart":true});
            var sketch = newSketch(context, id + "F4", { "sketchPlane" : qUnion([Q0])});
            skCircle(sketch, "E43", {"center": v(0, 0) * mm, "radius": 8 * mm});
            skSolve(sketch);
        }
        {
            var Q0;
            Q0=qSketchRegion(id+"F4",true);
            extrude(context, id + "F5", {"entities" : qUnion([Q0]), "operationType" : NewBodyOperationType.ADD, "depth" : 1.5 * mm});
        }
        {
            var Q0;
            Q0=makeQuery(id+"F5.opExtrude","CAP_FACE",FACE,{"disambiguationData":[OSD([sQuery(id+"F4.wireOp",EDGE,"E43")])],"isStart":false});
            var sketch = newSketch(context, id + "F6", { "sketchPlane" : qUnion([Q0])});
            skCircle(sketch, "E44", {"center": v(0, 0) * mm, "radius": 2.5 * mm});
            skSolve(sketch);
        }
        {
            var Q0;
            Q0=qSketchRegion(id+"F6",true);
            extrude(context, id + "F7", {"entities" : qUnion([Q0]), "operationType" : NewBodyOperationType.REMOVE, "endBound" : BoundingType.THROUGH_ALL, "oppositeDirection" : true, "depth" : 25 * mm});
        }
        {
            var Q0;
            Q0=qCreatedBy(makeId("Right.planeOp"),FACE);
            var sketch = newSketch(context, id + "F8", { "sketchPlane" : qUnion([Q0])});
            skCircle(sketch, "E45", {"center": v(0, 12) * mm, "radius": 1.5 * mm});
            skSolve(sketch);
        }
        {
            var Q0;
            Q0=qSketchRegion(id+"F8",true);
            extrude(context, id + "F9", {"entities" : qUnion([Q0]), "operationType" : NewBodyOperationType.REMOVE, "endBound" : BoundingType.THROUGH_ALL, "oppositeDirection" : true, "depth" : 25 * mm});
        }
        {
            var Q0;
            Q0=qCreatedBy(makeId("Top.planeOp"),FACE);
            var sketch = newSketch(context, id + "F10", { "sketchPlane" : qUnion([Q0])});
            skCircle(sketch, "E46", {"center": v(0, 0) * mm, "radius": 3.18 * mm});
            skSolve(sketch);
        }
        {
            var Q0;
            Q0 = qSketchRegion(id + "F10", true);
            extrude(context, id + "F11", {"entities" : qUnion([Q0]), "operationType" : NewBodyOperationType.REMOVE, "endBound" : BoundingType.SYMMETRIC, "depth" : 50.8 * mm, "offsetDistance" : 25 * mm});
        }
        {
            var Q0;
            Q0=makeQuery(id+"F5.opExtrude","CAP_FACE",FACE,{"disambiguationData":[OSD([sQuery(id+"F4.wireOp",EDGE,"E43")])],"isStart":false});
            var sketch = newSketch(context, id + "F12", { "sketchPlane" : qUnion([Q0])});
            skCircle(sketch, "E47.0.0", {"center": v(0, 0) * mm, "radius": 8 * mm});
            skSolve(sketch);
        }
        {
            var Q0;
            Q0 = qSketchRegion(id + "F12", true);
            var Q1;
            Q1=makeQuery(id+"F5.opExtrude","CAP_FACE",FACE,{"disambiguationData":[OSD([sQuery(id+"F4.wireOp",EDGE,"E43")])],"isStart":true});
            extrude(context, id + "F13", {"entities" : qUnion([Q0]), "operationType" : NewBodyOperationType.REMOVE, "endBound" : BoundingType.UP_TO_SURFACE, "oppositeDirection" : true, "depth" : 25.4 * mm, "endBoundEntityFace" : qUnion([Q1]), "offsetDistance" : 25.4 * mm});
        }
        {
            var Q0;
            Q0=qCreatedBy(makeId("Front.planeOp"),FACE);
            var sketch = newSketch(context, id + "F14", { "sketchPlane" : qUnion([Q0])});
            skLineSegment(sketch, "E48", {"start": v(3.18, 0) * mm, "end": v(6.14, 0) * mm});
            skLineSegment(sketch, "E49", {"start": v(6.14, 0) * mm, "end": v(8, -1.4) * mm});
            skLineSegment(sketch, "E50", {"start": v(8, -1.4) * mm, "end": v(8, -1.9) * mm});
            skLineSegment(sketch, "E51", {"start": v(8, -1.9) * mm, "end": v(3.17, -1.9) * mm});
            skLineSegment(sketch, "E52", {"start": v(3.18, -1.9) * mm, "end": v(3.18, 0) * mm});
            skLineSegment(sketch, "E53", {"start": v(0, 0) * mm, "end": v(0, -2.56) * mm, "construction": true});
            skSolve(sketch);
        }
        {
            var Q0;
            Q0 = qSketchRegion(id + "F14", true);
            var Q1;
            Q1=sQuery(id+"F14.wireOp",EDGE,"E53");
            revolve(context, id + "F15", {"operationType" : NewBodyOperationType.ADD, "entities" : qUnion([Q0]), "axis" : qUnion([Q1]), "revolveType" : RevolveType.FULL});
        }
        {
            var Q0;
            Q0=qCreatedBy(makeId("Front.planeOp"),FACE);
            var sketch = newSketch(context, id + "F16", { "sketchPlane" : qUnion([Q0])});
            skLineSegment(sketch, "E54.bottom", {"start": v(-9.44, 14.91) * mm, "end": v(10.15, 14.91) * mm});
            skLineSegment(sketch, "E54.top", {"start": v(-9.44, 16.5) * mm, "end": v(10.15, 16.5) * mm});
            skLineSegment(sketch, "E54.left", {"start": v(-9.44, 16.5) * mm, "end": v(-9.44, 14.91) * mm});
            skLineSegment(sketch, "E54.right", {"start": v(10.15, 16.5) * mm, "end": v(10.15, 14.91) * mm});
            skLineSegment(sketch, "E55.bottom", {"start": v(-9.96, -1.9) * mm, "end": v(10.98, -1.9) * mm});
            skLineSegment(sketch, "E55.top", {"start": v(-9.96, -0.76) * mm, "end": v(10.98, -0.76) * mm});
            skLineSegment(sketch, "E55.left", {"start": v(-9.96, -1.9) * mm, "end": v(-9.96, -0.76) * mm});
            skLineSegment(sketch, "E55.right", {"start": v(10.98, -1.9) * mm, "end": v(10.98, -0.76) * mm});
            skSolve(sketch);
        }
        {
            var Q0;
            Q0 = qSketchRegion(id + "F16", true);
            extrude(context, id + "F17", {"entities" : qUnion([Q0]), "operationType" : NewBodyOperationType.REMOVE, "endBound" : BoundingType.SYMMETRIC, "oppositeDirection" : true, "depth" : 25.4 * mm, "offsetDistance" : 25.4 * mm});
        }
        {
            var Q0;
            Q0=makeQuery(id+"F17.boolean.opBoolean","INTERSECT",EDGE,{"derivedFrom":[makeQuery(id+"F3.opExtrude","SWEPT_FACE",FACE,{"disambiguationData":[OSD([sQuery(id+"F2.wireOp",EDGE,"E42")])]}),makeQuery(id+"F17.opExtrude","SWEPT_FACE",FACE,{"disambiguationData":[OSD([sQuery(id+"F16.wireOp",EDGE,"E54.bottom")])]})]});
            chamfer(context, id + "F18", {"entities" : qUnion([Q0]), "width" : 1.27 * mm, "tangentPropagation" : true});
        }
        {
            var Q0;
            Q0=makeQuery(id+"F1.opExtrude","SWEPT_BODY",BODY,{"disambiguationData":[OSD([sQuery(id+"F0.wireOp",EDGE,"E15"),sQuery(id+"F0.wireOp",EDGE,"E16"),sQuery(id+"F0.wireOp",EDGE,"E17"),sQuery(id+"F0.wireOp",EDGE,"E18"),sQuery(id+"F0.wireOp",EDGE,"E19"),sQuery(id+"F0.wireOp",EDGE,"E20"),sQuery(id+"F0.wireOp",EDGE,"E21.1.0"),sQuery(id+"F0.wireOp",EDGE,"E21.1.2"),sQuery(id+"F0.wireOp",EDGE,"E21.1.3"),sQuery(id+"F0.wireOp",EDGE,"E21.1.4"),sQuery(id+"F0.wireOp",EDGE,"E21.1.5"),sQuery(id+"F0.wireOp",EDGE,"E22.3.2.0"),sQuery(id+"F0.wireOp",EDGE,"E22.5.2.0"),sQuery(id+"F0.wireOp",EDGE,"E22.9.2.0"),sQuery(id+"F0.wireOp",EDGE,"E22.13.2.0"),sQuery(id+"F0.wireOp",EDGE,"E22.17.2.0"),sQuery(id+"F0.wireOp",EDGE,"E22.3.3.0"),sQuery(id+"F0.wireOp",EDGE,"E22.5.3.0"),sQuery(id+"F0.wireOp",EDGE,"E22.9.3.0"),sQuery(id+"F0.wireOp",EDGE,"E22.13.3.0"),sQuery(id+"F0.wireOp",EDGE,"E22.17.3.0"),sQuery(id+"F0.wireOp",EDGE,"E22.3.4.0"),sQuery(id+"F0.wireOp",EDGE,"E22.5.4.0"),sQuery(id+"F0.wireOp",EDGE,"E22.9.4.0"),sQuery(id+"F0.wireOp",EDGE,"E22.13.4.0"),sQuery(id+"F0.wireOp",EDGE,"E22.17.4.0"),sQuery(id+"F0.wireOp",EDGE,"E22.3.5.0"),sQuery(id+"F0.wireOp",EDGE,"E22.5.5.0"),sQuery(id+"F0.wireOp",EDGE,"E22.9.5.0"),sQuery(id+"F0.wireOp",EDGE,"E22.13.5.0"),sQuery(id+"F0.wireOp",EDGE,"E22.17.5.0"),sQuery(id+"F0.wireOp",EDGE,"E22.3.6.0"),sQuery(id+"F0.wireOp",EDGE,"E22.5.6.0"),sQuery(id+"F0.wireOp",EDGE,"E22.9.6.0"),sQuery(id+"F0.wireOp",EDGE,"E22.13.6.0"),sQuery(id+"F0.wireOp",EDGE,"E22.17.6.0"),sQuery(id+"F0.wireOp",EDGE,"E22.3.7.0"),sQuery(id+"F0.wireOp",EDGE,"E22.5.7.0"),sQuery(id+"F0.wireOp",EDGE,"E22.9.7.0"),sQuery(id+"F0.wireOp",EDGE,"E22.13.7.0"),sQuery(id+"F0.wireOp",EDGE,"E22.17.7.0"),sQuery(id+"F0.wireOp",EDGE,"E22.3.8.0"),sQuery(id+"F0.wireOp",EDGE,"E22.5.8.0"),sQuery(id+"F0.wireOp",EDGE,"E22.9.8.0"),sQuery(id+"F0.wireOp",EDGE,"E22.13.8.0"),sQuery(id+"F0.wireOp",EDGE,"E22.17.8.0"),sQuery(id+"F0.wireOp",EDGE,"E22.3.9.0"),sQuery(id+"F0.wireOp",EDGE,"E22.5.9.0"),sQuery(id+"F0.wireOp",EDGE,"E22.9.9.0"),sQuery(id+"F0.wireOp",EDGE,"E22.13.9.0"),sQuery(id+"F0.wireOp",EDGE,"E22.17.9.0"),sQuery(id+"F0.wireOp",EDGE,"E22.3.10.0"),sQuery(id+"F0.wireOp",EDGE,"E22.5.10.0"),sQuery(id+"F0.wireOp",EDGE,"E22.9.10.0"),sQuery(id+"F0.wireOp",EDGE,"E22.13.10.0"),sQuery(id+"F0.wireOp",EDGE,"E22.17.10.0"),sQuery(id+"F0.wireOp",EDGE,"E22.3.11.0"),sQuery(id+"F0.wireOp",EDGE,"E22.5.11.0"),sQuery(id+"F0.wireOp",EDGE,"E22.9.11.0"),sQuery(id+"F0.wireOp",EDGE,"E22.13.11.0"),sQuery(id+"F0.wireOp",EDGE,"E22.17.11.0"),sQuery(id+"F0.wireOp",EDGE,"E22.3.12.0"),sQuery(id+"F0.wireOp",EDGE,"E22.5.12.0"),sQuery(id+"F0.wireOp",EDGE,"E22.9.12.0"),sQuery(id+"F0.wireOp",EDGE,"E22.13.12.0"),sQuery(id+"F0.wireOp",EDGE,"E22.17.12.0"),sQuery(id+"F0.wireOp",EDGE,"E22.3.13.0"),sQuery(id+"F0.wireOp",EDGE,"E22.5.13.0"),sQuery(id+"F0.wireOp",EDGE,"E22.9.13.0"),sQuery(id+"F0.wireOp",EDGE,"E22.13.13.0"),sQuery(id+"F0.wireOp",EDGE,"E22.17.13.0"),sQuery(id+"F0.wireOp",EDGE,"E22.3.14.0"),sQuery(id+"F0.wireOp",EDGE,"E22.5.14.0"),sQuery(id+"F0.wireOp",EDGE,"E22.9.14.0"),sQuery(id+"F0.wireOp",EDGE,"E22.13.14.0"),sQuery(id+"F0.wireOp",EDGE,"E22.17.14.0"),sQuery(id+"F0.wireOp",EDGE,"E22.3.15.0"),sQuery(id+"F0.wireOp",EDGE,"E22.5.15.0"),sQuery(id+"F0.wireOp",EDGE,"E22.9.15.0"),sQuery(id+"F0.wireOp",EDGE,"E22.13.15.0"),sQuery(id+"F0.wireOp",EDGE,"E22.17.15.0"),sQuery(id+"F0.wireOp",EDGE,"E22.3.16.0"),sQuery(id+"F0.wireOp",EDGE,"E22.5.16.0"),sQuery(id+"F0.wireOp",EDGE,"E22.9.16.0"),sQuery(id+"F0.wireOp",EDGE,"E22.13.16.0"),sQuery(id+"F0.wireOp",EDGE,"E22.17.16.0"),sQuery(id+"F0.wireOp",EDGE,"E22.3.17.0"),sQuery(id+"F0.wireOp",EDGE,"E22.5.17.0"),sQuery(id+"F0.wireOp",EDGE,"E22.9.17.0"),sQuery(id+"F0.wireOp",EDGE,"E22.13.17.0"),sQuery(id+"F0.wireOp",EDGE,"E22.17.17.0"),sQuery(id+"F0.wireOp",EDGE,"E22.3.18.0"),sQuery(id+"F0.wireOp",EDGE,"E22.5.18.0"),sQuery(id+"F0.wireOp",EDGE,"E22.9.18.0"),sQuery(id+"F0.wireOp",EDGE,"E22.13.18.0"),sQuery(id+"F0.wireOp",EDGE,"E22.17.18.0"),sQuery(id+"F0.wireOp",EDGE,"E22.3.19.0"),sQuery(id+"F0.wireOp",EDGE,"E22.5.19.0"),sQuery(id+"F0.wireOp",EDGE,"E22.9.19.0"),sQuery(id+"F0.wireOp",EDGE,"E22.13.19.0"),sQuery(id+"F0.wireOp",EDGE,"E22.17.19.0"),sQuery(id+"F0.wireOp",EDGE,"E23.trimOffspring"),sQuery(id+"F0.wireOp",EDGE,"E24.trimOffspring"),sQuery(id+"F0.wireOp",EDGE,"E25.trimOffspring"),sQuery(id+"F0.wireOp",EDGE,"E26.trimOffspring"),sQuery(id+"F0.wireOp",EDGE,"E27.trimOffspring"),sQuery(id+"F0.wireOp",EDGE,"E28.trimOffspring"),sQuery(id+"F0.wireOp",EDGE,"E29.trimOffspring"),sQuery(id+"F0.wireOp",EDGE,"E30.trimOffspring"),sQuery(id+"F0.wireOp",EDGE,"E31.trimOffspring"),sQuery(id+"F0.wireOp",EDGE,"E32.trimOffspring"),sQuery(id+"F0.wireOp",EDGE,"E33.trimOffspring"),sQuery(id+"F0.wireOp",EDGE,"E34.trimOffspring"),sQuery(id+"F0.wireOp",EDGE,"E35.trimOffspring"),sQuery(id+"F0.wireOp",EDGE,"E36.trimOffspring"),sQuery(id+"F0.wireOp",EDGE,"E37.trimOffspring"),sQuery(id+"F0.wireOp",EDGE,"E38.trimOffspring"),sQuery(id+"F0.wireOp",EDGE,"E39.trimOffspring"),sQuery(id+"F0.wireOp",EDGE,"E40.trimOffspring"),sQuery(id+"F0.wireOp",EDGE,"E41.trimOffspring")])]});
            transform(context, id + "F19", {"entities" : qUnion([Q0]), "transformType" : TransformType.TRANSLATION_3D, "dx" : 25.4 * mm, "dy" : 0 * mm, "dz" : 0 * mm, "makeCopy" : true});
        }
        {
            var Q0;
            Q0=makeQuery(id+"F19.opPattern","COPY",FACE,{"derivedFrom":makeQuery(id+"F17.boolean.opBoolean","COPY",FACE,{"derivedFrom":makeQuery(id+"F17.opExtrude","SWEPT_FACE",FACE,{"disambiguationData":[OSD([sQuery(id+"F16.wireOp",EDGE,"E54.bottom")])]})}),"instanceName":"1"});
            var sketch = newSketch(context, id + "F20", { "sketchPlane" : qUnion([Q0])});
            skCircle(sketch, "E56", {"center": v(25.4, 0) * mm, "radius": 13.37 * mm});
            skSolve(sketch);
        }
        {
            var Q0;
            Q0 = qSketchRegion(id + "F20", true);
            var Q1;
            Q1=makeQuery(id+"F19.opPattern","COPY",FACE,{"derivedFrom":makeQuery(id+"F3.opExtrude","CAP_FACE",FACE,{"disambiguationData":[OSD([sQuery(id+"F2.wireOp",EDGE,"E42")])],"isStart":true}),"instanceName":"1"});
            extrude(context, id + "F21", {"entities" : qUnion([Q0]), "operationType" : NewBodyOperationType.REMOVE, "endBound" : BoundingType.UP_TO_SURFACE, "oppositeDirection" : true, "depth" : 25.4 * mm, "endBoundEntityFace" : qUnion([Q1]), "offsetDistance" : 25.4 * mm});
        }
        {
            var Q0;
            Q0=makeQuery(id+"F19.opPattern","COPY",FACE,{"derivedFrom":makeQuery(id+"F17.boolean.opBoolean","COPY",FACE,{"derivedFrom":makeQuery(id+"F17.opExtrude","SWEPT_FACE",FACE,{"disambiguationData":[OSD([sQuery(id+"F16.wireOp",EDGE,"E55.top")])]})}),"instanceName":"1"});
            var sketch = newSketch(context, id + "F22", { "sketchPlane" : qUnion([Q0])});
            skCircle(sketch, "E57", {"center": v(25.4, 0) * mm, "radius": 11.23 * mm});
            skSolve(sketch);
        }
        {
            var Q0;
            Q0 = qSketchRegion(id + "F22", true);
            var Q1;
            Q1=makeQuery(id+"F19.opPattern","COPY",FACE,{"derivedFrom":makeQuery(id+"F15.opRevolve","SWEPT_FACE",FACE,{"disambiguationData":[OSD([sQuery(id+"F14.wireOp",EDGE,"E48")])]}),"instanceName":"1"});
            extrude(context, id + "F23", {"entities" : qUnion([Q0]), "operationType" : NewBodyOperationType.REMOVE, "endBound" : BoundingType.UP_TO_SURFACE, "oppositeDirection" : true, "depth" : 25.4 * mm, "endBoundEntityFace" : qUnion([Q1]), "offsetDistance" : 25.4 * mm});
        }
    });
